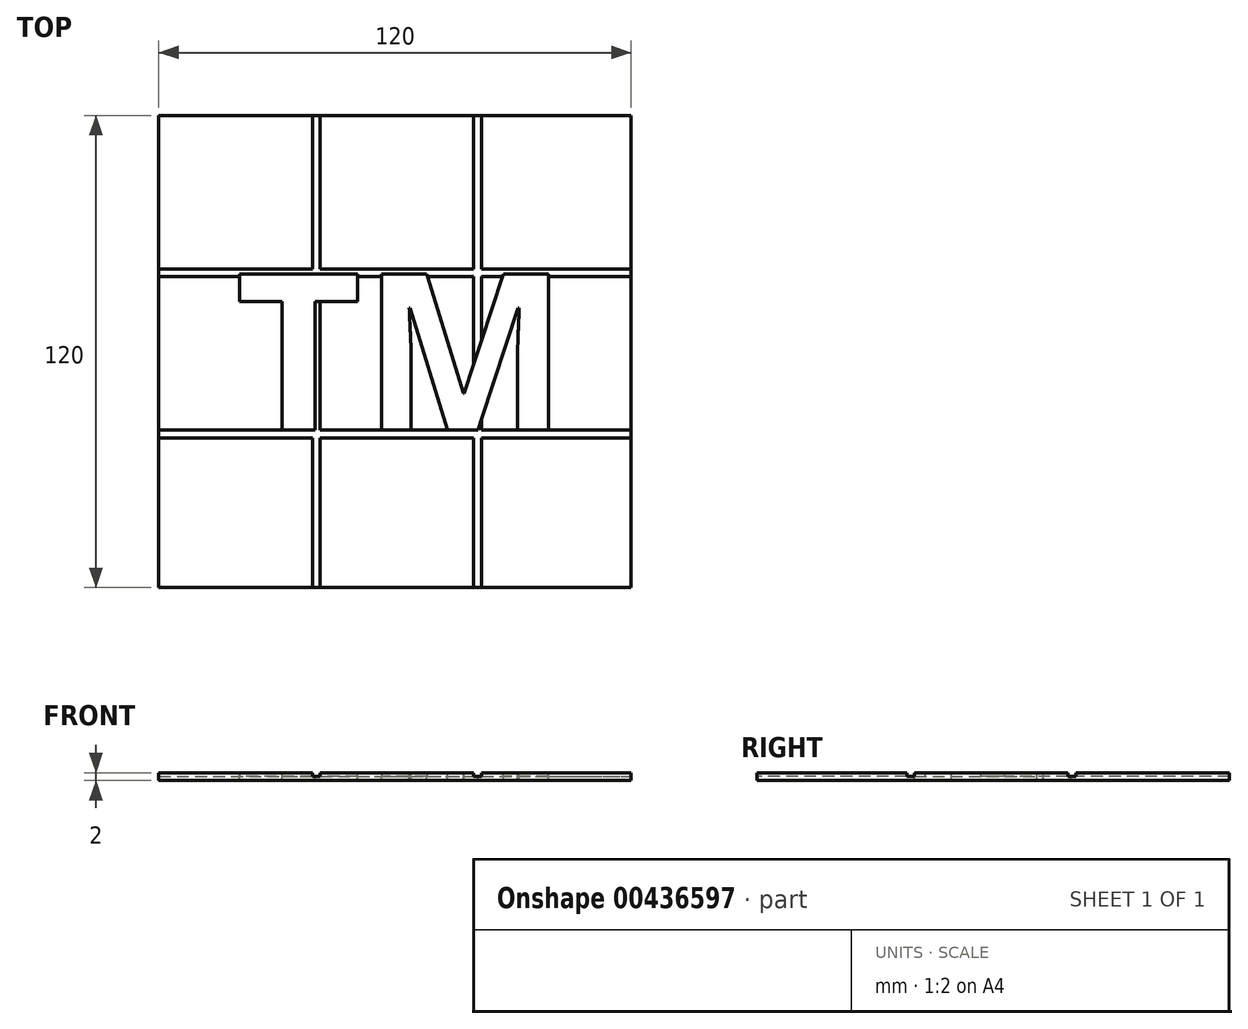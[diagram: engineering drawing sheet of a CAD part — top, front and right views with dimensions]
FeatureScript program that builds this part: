
annotation { "Feature Type Name" : "Feature", "Feature Type Description" : "" }
export const myFeature = defineFeature(function(context is Context, id is Id, definition is map)
    precondition{}
    {
        {
            var Q0;
            Q0=qCreatedBy(makeId("Top.planeOp"),FACE);
            var sketch = newSketch(context, id + "F0", { "sketchPlane" : qUnion([Q0])});
            skLineSegment(sketch, "E0.bottom", {"start": v(-61, 60) * mm, "end": v(59, 60) * mm});
            skLineSegment(sketch, "E0.top", {"start": v(-61, -60) * mm, "end": v(59, -60) * mm});
            skLineSegment(sketch, "E0.left", {"start": v(-61, 60) * mm, "end": v(-61, -60) * mm});
            skLineSegment(sketch, "E0.right", {"start": v(59, 60) * mm, "end": v(59, -60) * mm});
            skSolve(sketch);
        }
        {
            var Q0;
            Q0 = qSketchRegion(id + "F0", true);
            extrude(context, id + "F1", {"entities" : qUnion([Q0]), "depth" : 2 * mm});
        }
        {
            var Q0;
            Q0=makeQuery(id+"F1.opExtrude","CAP_FACE",FACE,{"disambiguationData":[OSD([sQuery(id+"F0.wireOp",EDGE,"E0.bottom"),sQuery(id+"F0.wireOp",EDGE,"E0.top"),sQuery(id+"F0.wireOp",EDGE,"E0.left"),sQuery(id+"F0.wireOp",EDGE,"E0.right")])],"isStart":false});
            var sketch = newSketch(context, id + "F2", { "sketchPlane" : qUnion([Q0])});
            skText(sketch, "E1", { "text": "TM", "fontName": "OpenSans-Bold.ttf"});
            const initialGuessF2  = {"E1": [-0.04158, -0.02, 1, 0, 0.04]};
            skSetInitialGuess(sketch, initialGuessF2);
            skSolve(sketch);
        }
        {
            var Q0;
            Q0 = qSketchRegion(id + "F2", true);
            extrude(context, id + "F3", {"entities" : qUnion([Q0]), "operationType" : NewBodyOperationType.REMOVE, "oppositeDirection" : true, "depth" : 25 * mm});
        }
        {
            var Q0;
            Q0=makeQuery(id+"F1.opExtrude","CAP_FACE",FACE,{"disambiguationData":[OSD([sQuery(id+"F0.wireOp",EDGE,"E0.bottom"),sQuery(id+"F0.wireOp",EDGE,"E0.top"),sQuery(id+"F0.wireOp",EDGE,"E0.left"),sQuery(id+"F0.wireOp",EDGE,"E0.right")])],"isStart":false});
            var sketch = newSketch(context, id + "F4", { "sketchPlane" : qUnion([Q0])});
            skLineSegment(sketch, "E2.bottom", {"start": v(-71, 21) * mm, "end": v(69, 21) * mm});
            skLineSegment(sketch, "E2.top", {"start": v(-71, 19) * mm, "end": v(69, 19) * mm});
            skLineSegment(sketch, "E2.left", {"start": v(-71, 21) * mm, "end": v(-71, 19) * mm});
            skLineSegment(sketch, "E2.right", {"start": v(69, 21) * mm, "end": v(69, 19) * mm});
            skLineSegment(sketch, "E3.bottom", {"start": v(-66.18, -20) * mm, "end": v(73.82, -20) * mm});
            skLineSegment(sketch, "E3.top", {"start": v(-66.18, -22) * mm, "end": v(73.82, -22) * mm});
            skLineSegment(sketch, "E3.left", {"start": v(-66.18, -20) * mm, "end": v(-66.18, -22) * mm});
            skLineSegment(sketch, "E3.right", {"start": v(73.82, -20) * mm, "end": v(73.82, -22) * mm});
            skLineSegment(sketch, "E4.bottom", {"start": v(-22, 67.2) * mm, "end": v(-20, 67.2) * mm});
            skLineSegment(sketch, "E4.top", {"start": v(-22, -71.42) * mm, "end": v(-20, -71.42) * mm});
            skLineSegment(sketch, "E4.left", {"start": v(-22, 67.2) * mm, "end": v(-22, -71.42) * mm});
            skLineSegment(sketch, "E4.right", {"start": v(-20, 67.2) * mm, "end": v(-20, -71.42) * mm});
            skLineSegment(sketch, "E5.bottom", {"start": v(19, 68.62) * mm, "end": v(21, 68.62) * mm});
            skLineSegment(sketch, "E5.left", {"start": v(19, 68.62) * mm, "end": v(19, -70) * mm});
            skLineSegment(sketch, "E5.right", {"start": v(21, 68.62) * mm, "end": v(21, -70) * mm});
            skLineSegment(sketch, "E6", {"start": v(19, -70) * mm, "end": v(21, -70) * mm});
            skSolve(sketch);
        }
        {
            var Q0;
            Q0 = qSketchRegion(id + "F4", true);
            extrude(context, id + "F5", {"entities" : qUnion([Q0]), "operationType" : NewBodyOperationType.REMOVE, "oppositeDirection" : true, "depth" : 1 * mm});
        }
    });
